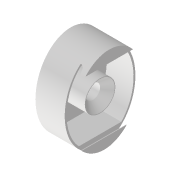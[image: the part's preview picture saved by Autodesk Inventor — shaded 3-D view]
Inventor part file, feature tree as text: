
AUTODESK INVENTOR PART (.ipt)
format: ipt  version: 2022 (Build 260153000, 153)  size: 529,408 bytes
history: native  units: mm
features: reference x7, extrude x6, sketch x6, projected_geometry x2, other x2, chamfer x1
ambient origin geometry x8: Origin, YZ Plane, XZ Plane, XY Plane, X Axis, Y Axis, Z Axis, Center Point
bodies: Volumenkörper1 (feature_tree)
feature tree (24):
  extrude  "Extrusion1"  Depth=0.2mm
  extrude  "Extrusion2"  Depth=0.1mm
  extrude  "Extrusion3"  Depth=0.2mm
  extrude  "Extrusion4"  Depth=24.0mm
  chamfer  "Fase1"  Distance=60.0mm
  extrude  "Extrusion5"  Depth=12.0mm
  extrude  "Extrusion6"  Depth=18.0mm TaperAngle=0.0deg
  sketch  "Skizze1"  dims[d0=0.2mm d1=0.2mm]
  reference  "Referenz1"
  reference  "Referenz2"
  reference  "Referenz3"
  reference  "Referenz4"
  reference  "Referenz5"
  reference  "Referenz6"
  sketch  "Skizze2"  dims[d3=0.1mm d4=0.1mm]
  reference  "Referenz9"
  sketch  "Skizze3"  dims[d5=0.1mm d7=0.2mm]
  sketch  "Skizze4"  dims[d8=6.0mm d9=24.0mm]
  sketch  "Skizze5"  dims[d10=6.0mm d11=60.0mm d12=0.0mm]
  projected_geometry  "Projizierte Kontur1"
  sketch  "Skizze6"  dims[d13=0.0mm d14=0.0mm d15=12.0mm d16=18.0mm d17=0.0mm d18=5.8mm d19=8.0mm d20=0.0mm d21=6.0mm d22=2.0mm d23=45.0deg d24=1.0mm d25=0.0mm d26=0.2mm d27=73.218841mm d28=36.60942mm d30=1.5mm d31=0.5mm d32=22.0mm d33=0.0mm]
  projected_geometry  "Projizierte Kontur2"
  other  "Spectroscope_v0.iam"
  other  "Spectrometer_gratingholder_v0:1"
